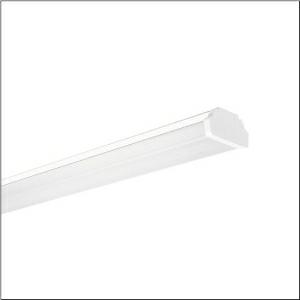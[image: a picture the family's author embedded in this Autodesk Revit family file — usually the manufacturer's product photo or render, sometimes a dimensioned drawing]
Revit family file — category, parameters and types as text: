
# Revit family: dus_31_gen_2_53bd813dv4a5c2_132e
name_source: partatom
category: Lighting Fixtures
units: mm (PartAtom-declared; Revit-internal decimal feet)

## family parameters
Cut with Voids When Loaded = No
Host = Face
Light Source = No
Part Type = Normal
Room Calculation Point = No
Round Connector Dimension = Use Diameter
Shared = No

## types (1)
- --- (1 x LED, 10610 lm, 61.4 W, 4000K)
    Apparent Load = 61 VA
    CIE Flux Codes = 62 83 95 93 100
    Color Rendering = 80
    Color Temperature = 4000K
    Default Elevation = 1800 mm
    Description = DUS 31 Gen.2, luminaire insert, of sheet steel, coil coated, white, length: 1.535mm, width: 81mm, height: 90mm, 5x system unit, system units: 307mm, LED rated luminous flux: 10.610lm, light colour: 840, SDCM (Standard Deviation of Colour Matching)MacAdam ≤ 3 SDCM (initial), control gear: DALI 2, control gear: ECG DALI, with plug, 5-pole, with phase selection, mains connection: 220..240V, AC, 50/60Hz, rated input power: 61W, through-wiring accessed according to module size, primary optical cover: cover, of PMMA, light emission: direct distribution, primary light characteristic: symmetric, protection rating (complete): IP20, protection rating (LED compartment): IP50, insulation class (complete): insulation class I (protective earthing), certification: CE, ENEC, VDE, UKCA, impact resistance: IK03, permissible ambient temperature for indoor applications: -25..+35°C, corresponds to IFS (International Featured Standards) requirements for safety and quality in the food industry, reducing of maximum allowable ambient temperature of 5°C with ceiling mounting, packaging unit: 1 piece
    Height = 95 mm
    Lamp = 1 x LED
    Lamp Light Flux = 10610 lm
    Lamp Power = 61.4 W
    Lamp count = 1
    Length = 1535 mm
    Luminous efficacy = 173 lm/W
    Manufacturer = Siteco
    ModVariant = No
    Model = 53BD813DV4A5C2
    Mounting Place = Ceiling
    Mounting Type = Pendant
    Number of Poles = 1
    OnlyDefault = Yes
    Power Factor = 1
    Product Name = DUS 31 Gen.2
    Product group = luminaire insert | ceiling pendant
    ProductGroupID = 901
    Protection Class = Protection class I
    Protection Degree = IP 20
    RLX_Detail_Level = 1
    RLX_Emergency_Light_Flux = 0 lm
    RLX_Emergency_Type = 0
    RLX_Emergency_Type_DB = No
    RlxData = <blob elided: 32441 chars, md5=555825b2>
    Socket = socket
    Standby Power = 0 W
    System Light Flux = 10610 lm
    System Power = 61 W
    Type Comments = factory setting: luminous flux: 100 % | dim-lin: 254 | 418 mA
    Type Image = l_1319596.jpg
    URL = http://relux.com
    VarID = @adj_050305
    Voltage = 0 V
    Weight = 0.00 kg
    Width = 81 mm

## geometry (parser evidence)
native form markers: Blend x4, Sweep x14
no freeform markers — native parametric forms only
